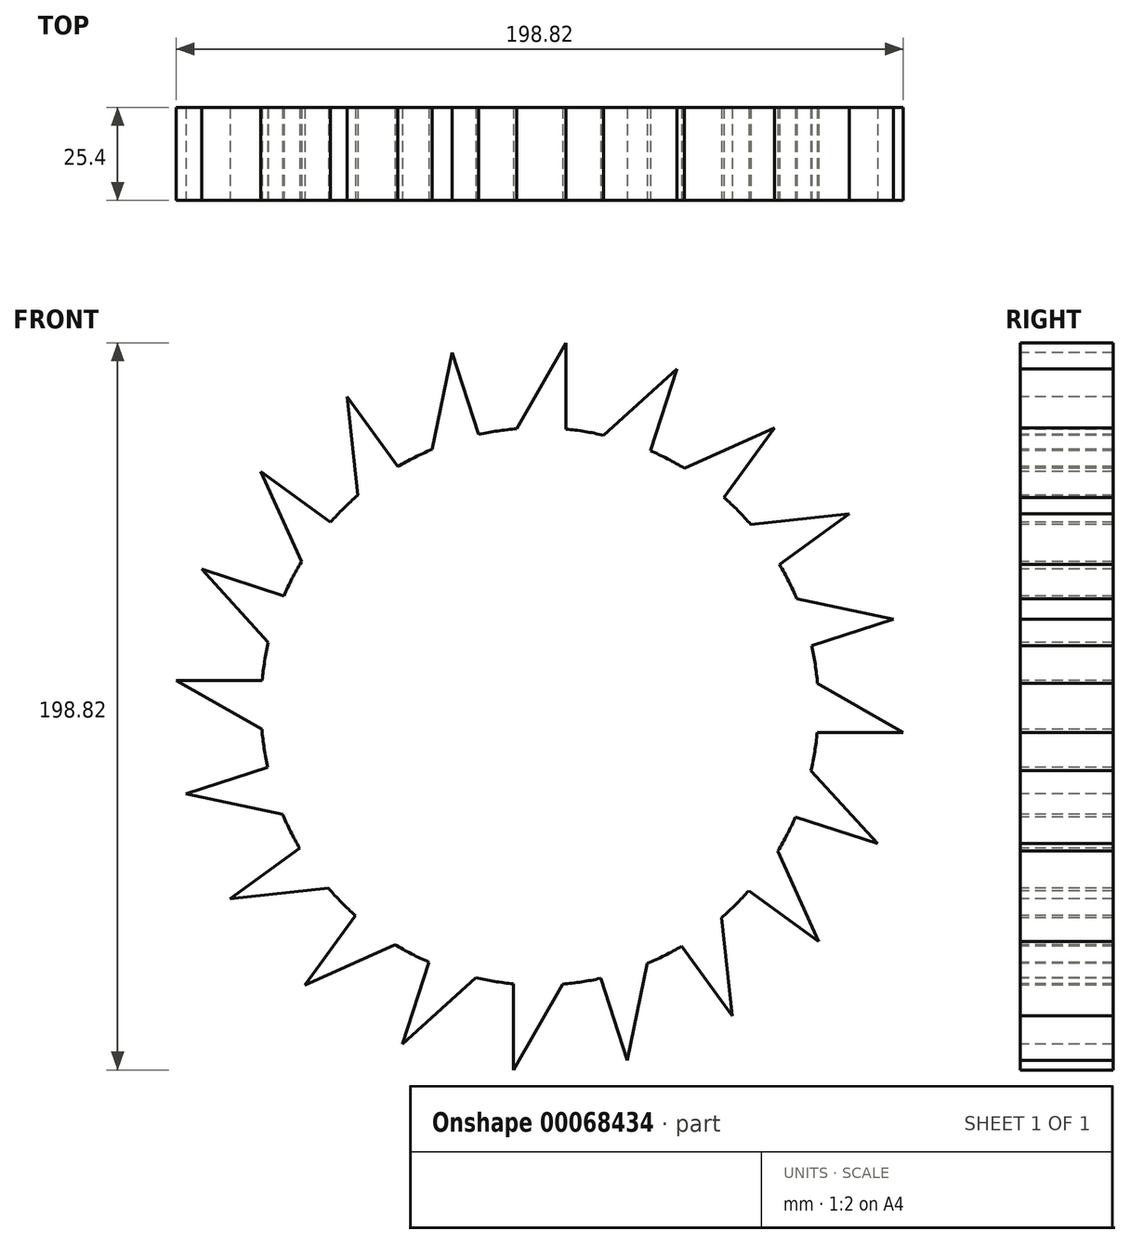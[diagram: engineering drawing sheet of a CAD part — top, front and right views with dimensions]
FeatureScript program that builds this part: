
annotation { "Feature Type Name" : "Feature", "Feature Type Description" : "" }
export const myFeature = defineFeature(function(context is Context, id is Id, definition is map)
    precondition{}
    {
        {
            var Q0;
            Q0=qCreatedBy(makeId("Front.planeOp"),FACE);
            var sketch = newSketch(context, id + "F0", { "sketchPlane" : qUnion([Q0])});
            skCircle(sketch, "E0", {"center": v(0, 0) * mm, "radius": 76.2 * mm});
            skSolve(sketch);
        }
        {
            var Q0;
            Q0=makeQuery(id+"F0.imprint","IMPRINT",FACE,{"disambiguationData":[TD([[makeQuery(id+"F0.imprint","IMPRINT",EDGE,{"derivedFrom":sQuery(id+"F0.wireOp",EDGE,"E0")}),1.0]])]});
            extrude(context, id + "F1", {"entities" : qUnion([Q0]), "depth" : 25.4 * mm});
        }
        {
            var Q0;
            Q0=makeQuery(id+"F1.opExtrude","CAP_FACE",FACE,{"disambiguationData":[OSD([sQuery(id+"F0.wireOp",EDGE,"E0")])],"isStart":false});
            var sketch = newSketch(context, id + "F2", { "sketchPlane" : qUnion([Q0])});
            skLineSegment(sketch, "E1", {"start": v(-6.27, 75.94) * mm, "end": v(7.15, 99.41) * mm});
            skLineSegment(sketch, "E2", {"start": v(7.15, 99.41) * mm, "end": v(7.15, 75.86) * mm});
            skLineSegment(sketch, "E3", {"start": v(7.15, 75.86) * mm, "end": v(-6.27, 75.94) * mm});
            skSolve(sketch);
        }
        {
            var Q0;
            Q0 = qSketchRegion(id + "F2", true);
            var Q1;
            Q1=makeQuery(id+"F1.opExtrude","CAP_FACE",FACE,{"disambiguationData":[OSD([sQuery(id+"F0.wireOp",EDGE,"E0")])],"isStart":true});
            extrude(context, id + "F3", {"entities" : qUnion([Q0]), "operationType" : NewBodyOperationType.ADD, "endBound" : BoundingType.UP_TO_SURFACE, "oppositeDirection" : true, "endBoundEntityFace" : qUnion([Q1]), "depth" : 25.4 * mm});
        }
        {
            var Q0;
            Q0=makeQuery(id+"F1.opExtrude","SWEPT_BODY",BODY,{"disambiguationData":[OSD([sQuery(id+"F0.wireOp",EDGE,"E0")])]});
            var Q1;
            Q1=makeQuery(id+"F1.opExtrude","SWEPT_FACE",FACE,{"disambiguationData":[OSD([sQuery(id+"F0.wireOp",EDGE,"E0")])]});
            circularPattern(context, id + "F4", {"operationType" : NewBodyOperationType.ADD, "entities" : qUnion([Q0]), "axis" : qUnion([Q1]), "angle" : 360 * degree, "instanceCount" : 20, "equalSpace" : true});
        }
    });
